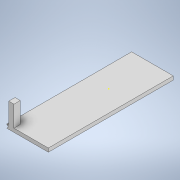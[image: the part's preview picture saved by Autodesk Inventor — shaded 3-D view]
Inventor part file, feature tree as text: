
AUTODESK INVENTOR PART (.ipt)
format: ipt  version: 2020 (Build 240168000, 168)  size: 135,168 bytes
history: native  units: mm
features: sketch x6, extrude x4
ambient origin geometry x8: Origin, YZ Plane, XZ Plane, XY Plane, X Axis, Y Axis, Z Axis, Center Point
bodies: Solid1 (feature_tree)
feature tree (10):
  extrude  "Extrusion1"  Depth=84.0mm
  extrude  "Extrusion2"  Depth=20.0mm
  sketch  "Sketch4"  dims[d4=3.5mm d5=0.0mm d10=1.5mm]
  extrude  "Extrusion3"  Depth=3.5mm
  sketch  "Sketch6"  dims[d15=7.0mm]
  extrude  "Extrusion4"  Depth=36.0mm TaperAngle=0.0deg
  sketch  "Sketch1"  dims[d0=40.0mm d1=84.0mm]
  sketch  "Sketch3"  dims[d2=20.0mm d3=42.0mm]
  sketch  "Sketch5"  dims[d11=127.5mm d12=0.0mm d13=36.0mm d14=0.0mm]
  sketch  "Sketch7"  dims[d16=6.0mm d17=20.0mm d18=0.0mm]
